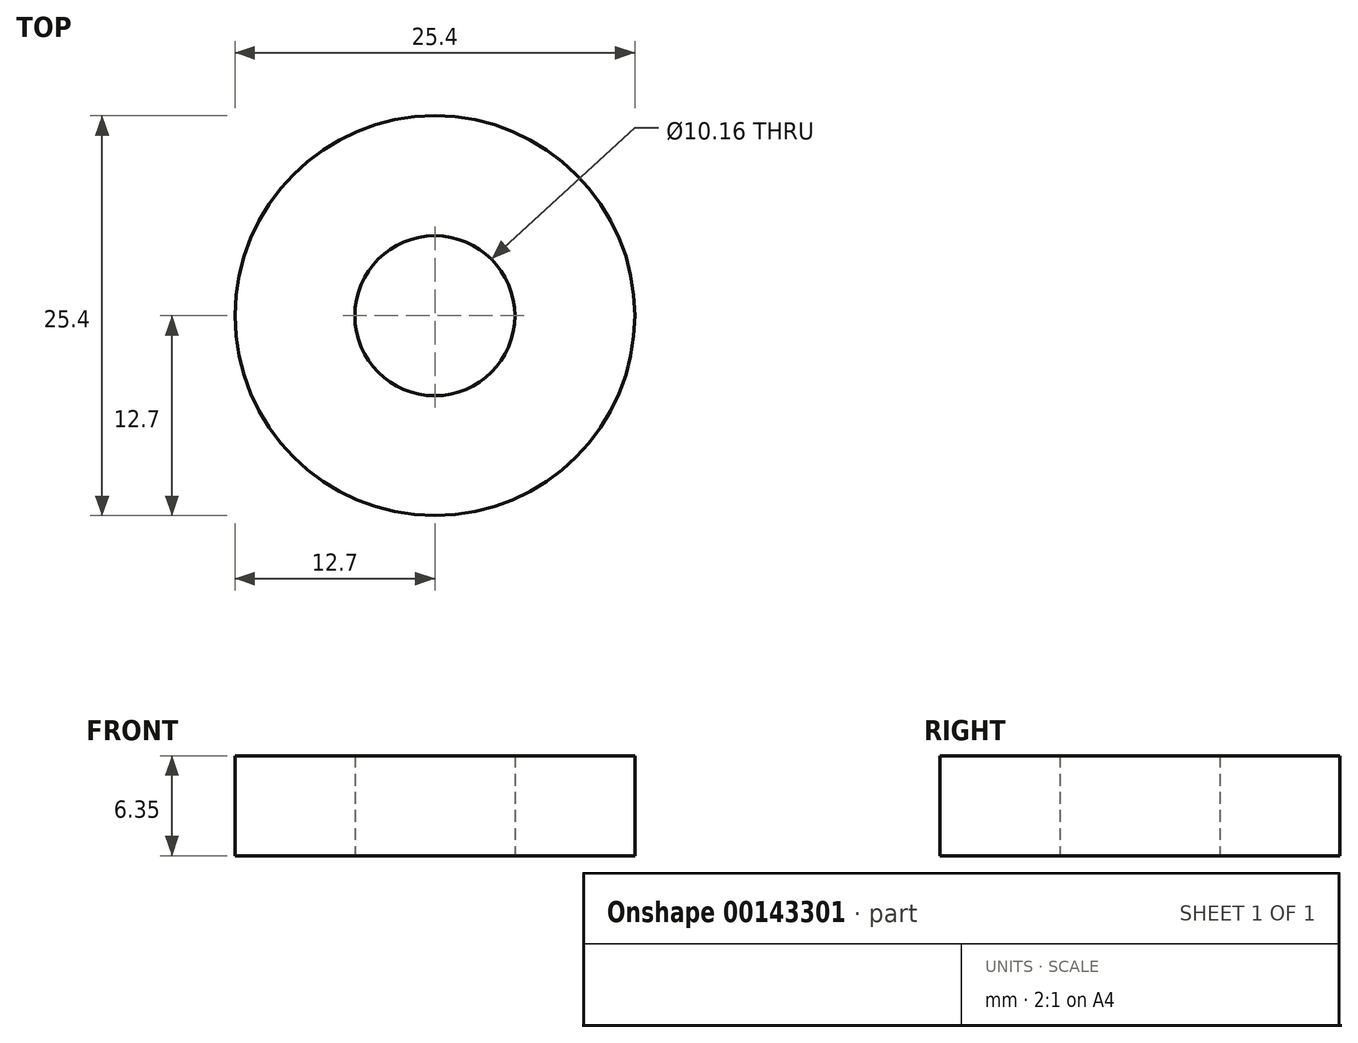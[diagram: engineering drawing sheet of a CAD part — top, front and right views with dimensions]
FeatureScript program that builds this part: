
annotation { "Feature Type Name" : "Feature", "Feature Type Description" : "" }
export const myFeature = defineFeature(function(context is Context, id is Id, definition is map)
    precondition{}
    {
        {
            var Q0;
            Q0=qCreatedBy(makeId("Top.planeOp"),FACE);
            var sketch = newSketch(context, id + "F0", { "sketchPlane" : qUnion([Q0])});
            skCircle(sketch, "E0", {"center": v(0, 0) * mm, "radius": 5.08 * mm});
            skCircle(sketch, "E1", {"center": v(0, 0) * mm, "radius": 12.7 * mm});
            skSolve(sketch);
        }
        {
            var Q0;
            Q0 = qSketchRegion(id + "F0", true);
            extrude(context, id + "F1", {"entities" : qUnion([Q0]), "depth" : 6.35 * mm});
        }
    });
